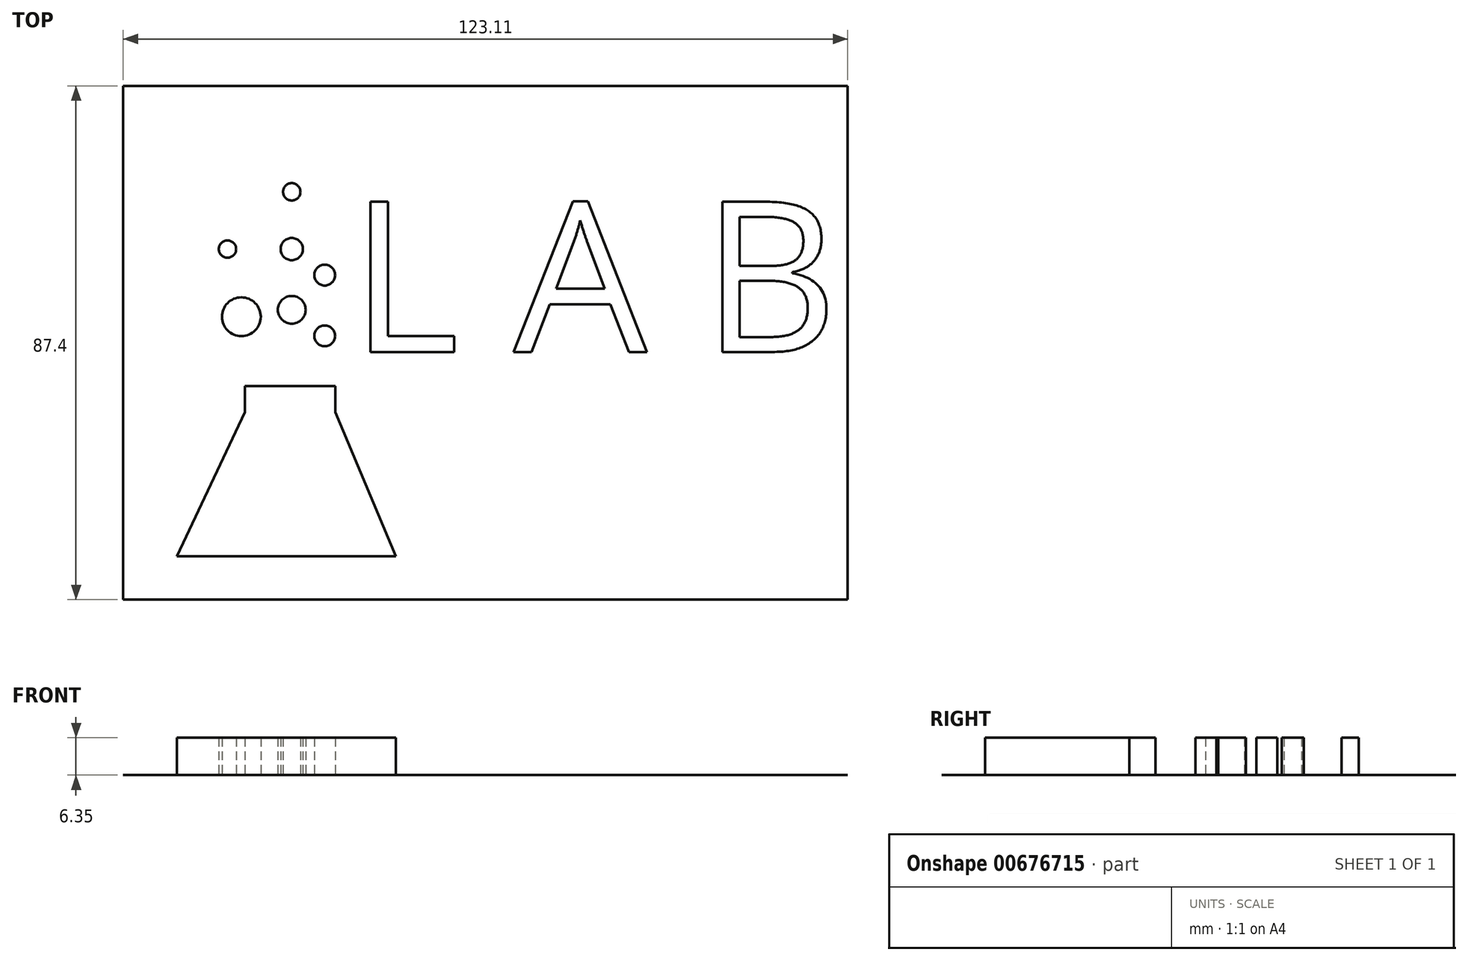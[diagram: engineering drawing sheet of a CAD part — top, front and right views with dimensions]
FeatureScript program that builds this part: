
annotation { "Feature Type Name" : "Feature", "Feature Type Description" : "" }
export const myFeature = defineFeature(function(context is Context, id is Id, definition is map)
    precondition{}
    {
        {
            var Q0;
            Q0=qCreatedBy(makeId("Top.planeOp"),FACE);
            var sketch = newSketch(context, id + "F0", { "sketchPlane" : qUnion([Q0])});
            skLineSegment(sketch, "E0.bottom", {"start": v(-59.56, 45.25) * mm, "end": v(63.55, 45.25) * mm});
            skLineSegment(sketch, "E0.top", {"start": v(-59.56, -42.15) * mm, "end": v(63.55, -42.15) * mm});
            skLineSegment(sketch, "E0.left", {"start": v(-59.56, 45.25) * mm, "end": v(-59.56, -42.15) * mm});
            skLineSegment(sketch, "E0.right", {"start": v(63.55, 45.25) * mm, "end": v(63.55, -42.15) * mm});
            skSolve(sketch);
        }
        {
            var Q0;
            Q0 = qSketchRegion(id + "F0", true);
            extrude(context, id + "F1", {"entities" : qUnion([Q0]), "depth" : 1 / 203.2 * mm, "offsetDistance" : 25.4 * mm});
        }
        {
            var Q0;
            Q0=qCreatedBy(makeId("Top.planeOp"),FACE);
            var sketch = newSketch(context, id + "F2", { "sketchPlane" : qUnion([Q0])});
            skLineSegment(sketch, "E1", {"start": v(-50.41, -34.76) * mm, "end": v(-13.21, -34.76) * mm});
            skLineSegment(sketch, "E2", {"start": v(-50.41, -34.76) * mm, "end": v(-38.9, -10.26) * mm});
            skLineSegment(sketch, "E3", {"start": v(-13.21, -34.76) * mm, "end": v(-23.55, -10.26) * mm});
            skLineSegment(sketch, "E4", {"start": v(-38.9, -10.26) * mm, "end": v(-23.55, -10.26) * mm});
            skLineSegment(sketch, "E5", {"start": v(-38.9, -10.26) * mm, "end": v(-38.9, -5.83) * mm});
            skLineSegment(sketch, "E6", {"start": v(-38.9, -5.83) * mm, "end": v(-23.55, -5.83) * mm});
            skLineSegment(sketch, "E7", {"start": v(-23.55, -5.83) * mm, "end": v(-23.55, -10.26) * mm});
            skCircle(sketch, "E8", {"center": v(-41.85, 17.5) * mm, "radius": 1.48 * mm});
            skCircle(sketch, "E9", {"center": v(-30.93, 27.24) * mm, "radius": 1.48 * mm});
            skCircle(sketch, "E10", {"center": v(-25.32, 2.73) * mm, "radius": 1.77 * mm});
            skCircle(sketch, "E11", {"center": v(-30.93, 17.5) * mm, "radius": 1.9 * mm});
            skCircle(sketch, "E12", {"center": v(-39.49, 5.98) * mm, "radius": 3.3 * mm});
            skCircle(sketch, "E13", {"center": v(-25.32, 13.06) * mm, "radius": 1.77 * mm});
            skCircle(sketch, "E14", {"center": v(-30.93, 7.16) * mm, "radius": 2.36 * mm});
            skSolve(sketch);
        }
        {
            var Q0;
            Q0=makeQuery(id+"F1.opExtrude","CAP_FACE",FACE,{"disambiguationData":[OSD([sQuery(id+"F0.wireOp",EDGE,"E0.bottom"),sQuery(id+"F0.wireOp",EDGE,"E0.top"),sQuery(id+"F0.wireOp",EDGE,"E0.left"),sQuery(id+"F0.wireOp",EDGE,"E0.right")])],"isStart":false});
            var sketch = newSketch(context, id + "F3", { "sketchPlane" : qUnion([Q0])});
            skText(sketch, "E15", { "text": "L A B", "fontName": "OpenSans-Regular.ttf"});
            const initialGuessF3  = {"E15": [-0.02107, 0, 1, 0, 0.02576]};
            skSetInitialGuess(sketch, initialGuessF3);
            skSolve(sketch);
        }
        {
            var Q0;
            Q0 = qSketchRegion(id + "F2", true);
            extrude(context, id + "F4", {"entities" : qUnion([Q0]), "operationType" : NewBodyOperationType.ADD, "depth" : 6.35 * mm, "offsetDistance" : 25.4 * mm});
        }
        {
            var Q0;
            Q0 = qSketchRegion(id + "F3", true);
            extrude(context, id + "F5", {"entities" : qUnion([Q0]), "operationType" : NewBodyOperationType.ADD, "depth" : 1 / 203.2 * mm, "offsetDistance" : 25.4 * mm});
        }
    });
